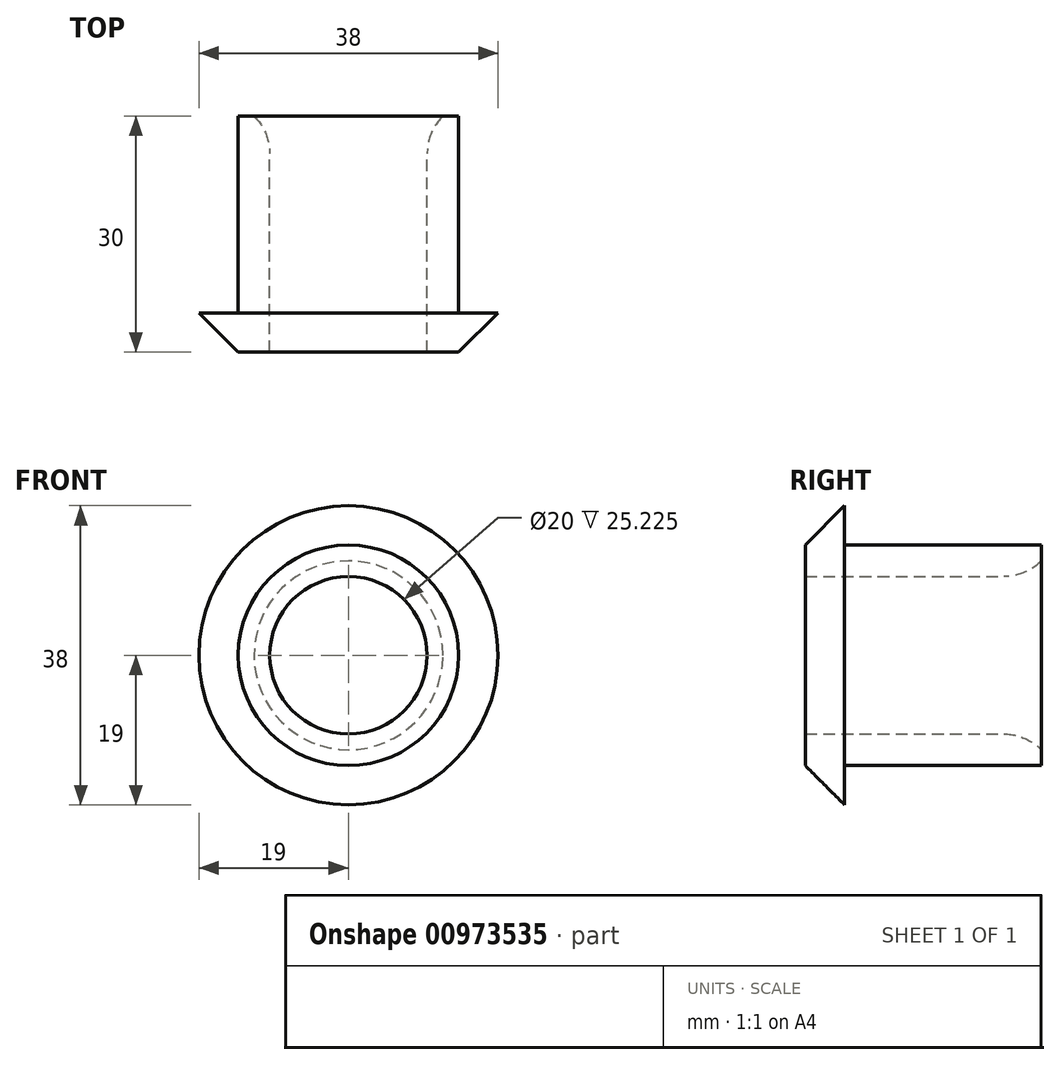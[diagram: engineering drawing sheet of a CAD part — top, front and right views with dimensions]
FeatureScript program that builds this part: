
annotation { "Feature Type Name" : "Feature", "Feature Type Description" : "" }
export const myFeature = defineFeature(function(context is Context, id is Id, definition is map)
    precondition{}
    {
        {
            var Q0;
            Q0=qCreatedBy(makeId("Front.planeOp"),FACE);
            var sketch = newSketch(context, id + "F0", { "sketchPlane" : qUnion([Q0])});
            skCircle(sketch, "E0", {"center": v(0, 0) * mm, "radius": 19 * mm});
            skCircle(sketch, "E1", {"center": v(0, 0) * mm, "radius": 14 * mm});
            skCircle(sketch, "E2", {"center": v(0, 0) * mm, "radius": 10 * mm});
            skSolve(sketch);
        }
        {
            var Q0;
            Q0 = qSketchRegion(id + "F0", true);
            var Q1;
            Q1=makeQuery(id+"F0.imprint","IMPRINT",FACE,{"disambiguationData":[TD([[makeQuery(id+"F0.imprint","IMPRINT",EDGE,{"derivedFrom":sQuery(id+"F0.wireOp",EDGE,"E1")}),1.0]])]});
            extrude(context, id + "F1", {"entities" : qUnion([Q0, Q1]), "depth" : 5 * mm, "offsetDistance" : 25 * mm});
        }
        {
            var Q0;
            Q0=makeQuery(id+"F0.imprint","IMPRINT",FACE,{"disambiguationData":[TD([[makeQuery(id+"F0.imprint","IMPRINT",EDGE,{"derivedFrom":sQuery(id+"F0.wireOp",EDGE,"E1")}),1.0]])]});
            extrude(context, id + "F2", {"entities" : qUnion([Q0]), "operationType" : NewBodyOperationType.ADD, "oppositeDirection" : true, "depth" : 25 * mm, "offsetDistance" : 25 * mm});
        }
        {
            var Q0;
            Q0=makeQuery(id+"F1.opExtrude","CAP_EDGE",EDGE,{"disambiguationData":[OSD([sQuery(id+"F0.wireOp",EDGE,"E0")])],"isStart":false});
            chamfer(context, id + "F3", {"entities" : qUnion([Q0]), "width" : 5 * mm, "tangentPropagation" : true});
        }
        {
            var Q0;
            Q0=makeQuery(id+"F2.opExtrude","CAP_EDGE",EDGE,{"disambiguationData":[OSD([sQuery(id+"F0.wireOp",EDGE,"E2")])],"isStart":false});
            chamfer(context, id + "F4", {"entities" : qUnion([Q0]), "width" : 2 * mm, "tangentPropagation" : true});
        }
        {
            var Q0;
            {var subQ0=sQuery(id+"F0.wireOp",EDGE,"E2");Q0=makeQuery(id+"F4.opChamfer","BLEND_EDGE",EDGE,{"blendedFrom":[makeQuery(id+"F2.opExtrude","CAP_EDGE",EDGE,{"disambiguationData":[OSD([subQ0])],"isStart":false}),makeQuery(id+"F2.boolean.opBoolean","MERGE",FACE,{"derivedFrom":[makeQuery(id+"F1.opExtrude","SWEPT_FACE",FACE,{"disambiguationData":[OSD([subQ0])]}),makeQuery(id+"F2.opExtrude","SWEPT_FACE",FACE,{"disambiguationData":[OSD([subQ0])]})]})],"blendedInto":[makeQuery(id+"F2.boolean.opBoolean","MERGE",FACE,{"derivedFrom":[makeQuery(id+"F1.opExtrude","SWEPT_FACE",FACE,{"disambiguationData":[OSD([subQ0])]}),makeQuery(id+"F2.opExtrude","SWEPT_FACE",FACE,{"disambiguationData":[OSD([subQ0])]})]})]});}
            fillet(context, id + "F5", {"entities" : qUnion([Q0]), "radius" : 6.7 * mm, "tangentPropagation" : true, "allowEdgeOverflow" : false});
        }
    });
